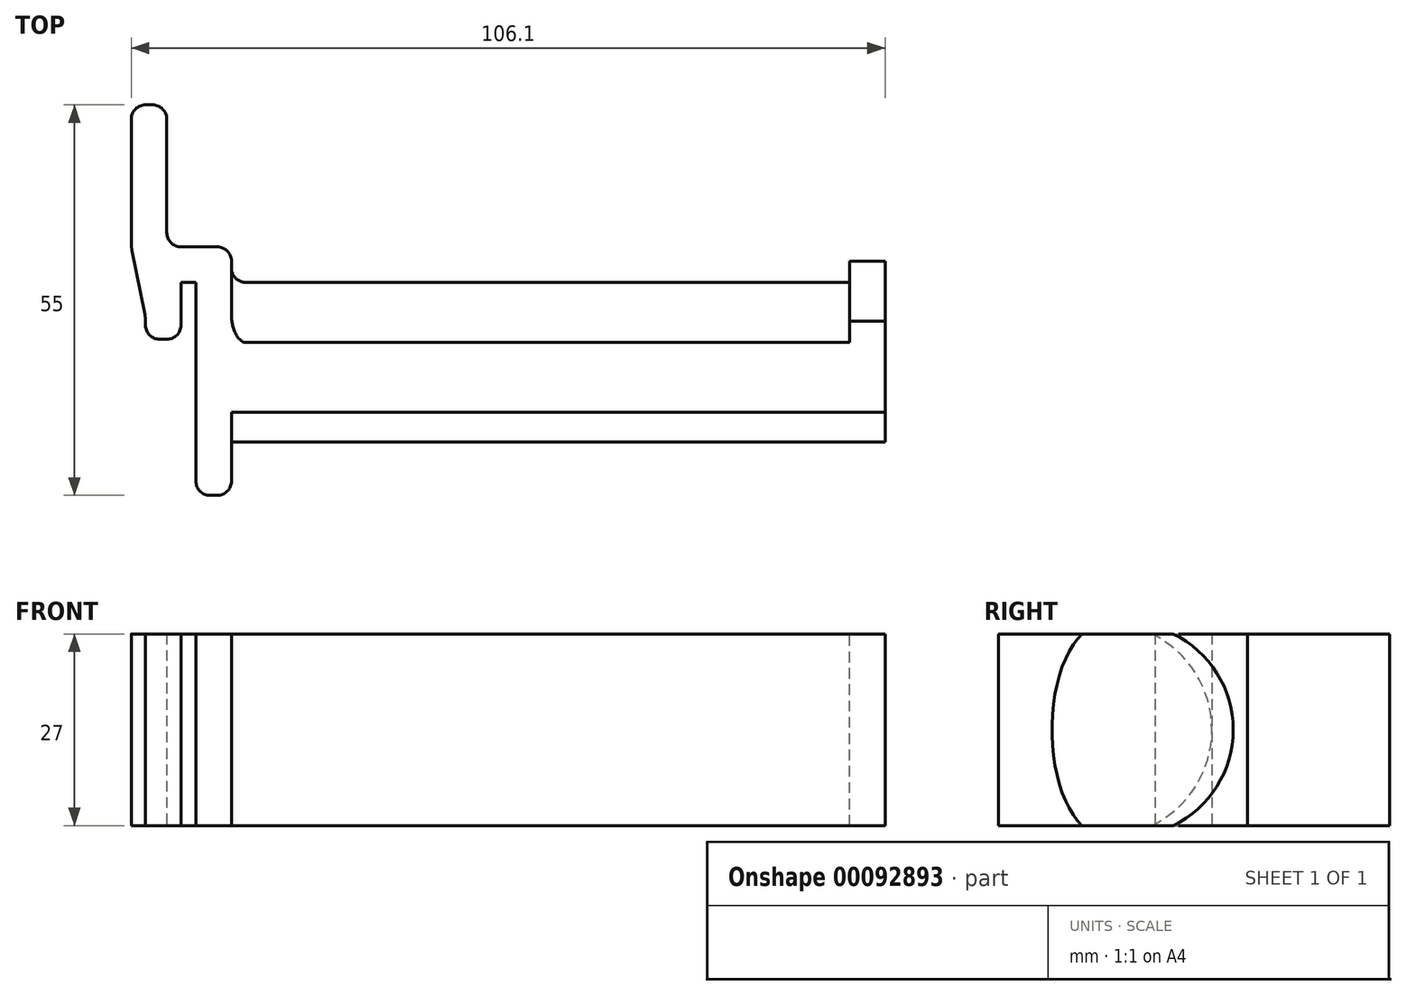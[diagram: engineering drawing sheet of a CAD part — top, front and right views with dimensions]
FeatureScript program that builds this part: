
annotation { "Feature Type Name" : "Feature", "Feature Type Description" : "" }
export const myFeature = defineFeature(function(context is Context, id is Id, definition is map)
    precondition{}
    {
        {
            assignVariable(context, id + "F0", {"name" : "Diameter", "anyValue" : 30});
        }
        {
            assignVariable(context, id + "F1", {"name" : "Width", "anyValue" : 85});
        }
        {
            var Q0;
            Q0=qCreatedBy(makeId("Top.planeOp"),FACE);
            var sketch = newSketch(context, id + "F2", { "sketchPlane" : qUnion([Q0])});
            skLineSegment(sketch, "E0", {"start": v(-10.1, -13) * mm, "end": v(-9.1, -13) * mm});
            skLineSegment(sketch, "E1", {"start": v(-7.1, -11) * mm, "end": v(-7.1, -5) * mm});
            skLineSegment(sketch, "E2", {"start": v(-7.1, -5) * mm, "end": v(-5, -5) * mm});
            skLineSegment(sketch, "E3", {"start": v(-5, -5) * mm, "end": v(-5, -33) * mm});
            skLineSegment(sketch, "E4", {"start": v(-3, -35) * mm, "end": v(-2, -35) * mm});
            skLineSegment(sketch, "E5", {"start": v(0, -33) * mm, "end": v(0, -2) * mm});
            skLineSegment(sketch, "E6", {"start": v(-2, 0) * mm, "end": v(-7.1, 0) * mm});
            skLineSegment(sketch, "E7", {"start": v(-9.1, 2) * mm, "end": v(-9.1, 18) * mm});
            skLineSegment(sketch, "E8", {"start": v(-11.1, 20) * mm, "end": v(-12.1, 20) * mm});
            skLineSegment(sketch, "E9", {"start": v(-14.1, 18) * mm, "end": v(-14.1, 0.5) * mm});
            skLineSegment(sketch, "E10", {"start": v(-12.1, -10.5) * mm, "end": v(-12.1, -11) * mm});
            skPoint(sketch, "E11.visualSharp", {"position": v(-9.1, 0) * mm});
            skArc(sketch, "E11.filletArc", {"start": v(-9.1, 2) * mm, "mid": v(-8.51, 0.59) * mm, "end": v(-7.1, 0) * mm});
            skPoint(sketch, "E12.visualSharp", {"position": v(0, 0) * mm});
            skArc(sketch, "E12.filletArc", {"start": v(0, -2) * mm, "mid": v(-0.59, -0.59) * mm, "end": v(-2, 0) * mm});
            skPoint(sketch, "E13.visualSharp", {"position": v(-9.1, 20) * mm});
            skArc(sketch, "E13.filletArc", {"start": v(-9.1, 18) * mm, "mid": v(-9.69, 19.41) * mm, "end": v(-11.1, 20) * mm});
            skPoint(sketch, "E14.visualSharp", {"position": v(-14.1, 20) * mm});
            skArc(sketch, "E14.filletArc", {"start": v(-12.1, 20) * mm, "mid": v(-13.51, 19.41) * mm, "end": v(-14.1, 18) * mm});
            skPoint(sketch, "E15.visualSharp", {"position": v(0, -35) * mm});
            skArc(sketch, "E15.filletArc", {"start": v(-2, -35) * mm, "mid": v(-0.59, -34.41) * mm, "end": v(0, -33) * mm});
            skPoint(sketch, "E16.visualSharp", {"position": v(-5, -35) * mm});
            skArc(sketch, "E16.filletArc", {"start": v(-5, -33) * mm, "mid": v(-4.41, -34.41) * mm, "end": v(-3, -35) * mm});
            skPoint(sketch, "E17.visualSharp", {"position": v(-7.1, -13) * mm});
            skArc(sketch, "E17.filletArc", {"start": v(-9.1, -13) * mm, "mid": v(-7.69, -12.41) * mm, "end": v(-7.1, -11) * mm});
            skPoint(sketch, "E18.visualSharp", {"position": v(-12.1, -13) * mm});
            skArc(sketch, "E18.filletArc", {"start": v(-12.1, -11) * mm, "mid": v(-11.51, -12.41) * mm, "end": v(-10.1, -13) * mm});
            skLineSegment(sketch, "E19", {"start": v(-14, -0.49) * mm, "end": v(-12.2, -9.51) * mm});
            skPoint(sketch, "E20", {"position": v(-13.1, -5) * mm});
            skPoint(sketch, "E21.visualSharp", {"position": v(-14.1, 0) * mm});
            skArc(sketch, "E21.filletArc", {"start": v(-14.1, 0.5) * mm, "mid": v(-14.08, 0) * mm, "end": v(-14, -0.49) * mm});
            skPoint(sketch, "E22.visualSharp", {"position": v(-12.1, -10) * mm});
            skArc(sketch, "E22.filletArc", {"start": v(-12.1, -10.5) * mm, "mid": v(-12.12, -10) * mm, "end": v(-12.2, -9.51) * mm});
            skSolve(sketch);
        }
        {
            var Q0;
            Q0 = qSketchRegion(id + "F2", true);
            extrude(context, id + "F3", {"entities" : qUnion([Q0]), "endBound" : BoundingType.SYMMETRIC, "depth" : (getVariable(context, 'Diameter') * 0.9) * mm});
        }
        {
            var Q0;
            Q0=makeQuery(id+"F3.opExtrude","SWEPT_FACE",FACE,{"disambiguationData":[OSD([sQuery(id+"F2.wireOp",EDGE,"E5")])]});
            var sketch = newSketch(context, id + "F4", { "sketchPlane" : qUnion([Q0])});
            skArc(sketch, "E23", {"start": v(-13.46, -13.5) * mm, "mid": v(-5, 0) * mm, "end": v(-13.46, 13.5) * mm});
            skEllipse(sketch, "E24", {"center": v(-20, 0) * mm, "majorRadius": 15 * mm, "minorRadius": 7.5 * mm, "majorAxis": v(0, -1)});
            skLineSegment(sketch, "E25", {"start": v(-13.46, 13.5) * mm, "end": v(-23.27, 13.5) * mm});
            skLineSegment(sketch, "E26", {"start": v(-13.46, -13.5) * mm, "end": v(-23.27, -13.5) * mm});
            skSolve(sketch);
        }
        {
            var Q0;
            {var subQ0=sQuery(id+"F4.wireOp",EDGE,"E25");var subQ1=sQuery(id+"F4.wireOp",EDGE,"E24");var subQ2=makeQuery(id+"F4.imprint","INTERSECT",VERTEX,{"derivedFrom":[subQ1,subQ0]});Q0=makeQuery(id+"F4.imprint","IMPRINT",FACE,{"disambiguationData":[TD([[makeQuery(id+"F4.imprint","IMPRINT",EDGE,{"disambiguationData":[TD([[subQ2,1.0]])],"derivedFrom":subQ1}),1.0]])]});}
            var Q1;
            {var subQ0=sQuery(id+"F4.wireOp",EDGE,"E23");Q1=makeQuery(id+"F4.imprint","IMPRINT",FACE,{"disambiguationData":[TD([[makeQuery(id+"F4.imprint","IMPRINT",EDGE,{"derivedFrom":subQ0}),1.0]])]});}
            extrude(context, id + "F5", {"entities" : qUnion([Q0, Q1]), "operationType" : NewBodyOperationType.ADD, "depth" : (getVariable(context, 'Width') + 7) * mm});
        }
        {
            var Q0;
            Q0=makeQuery(id+"F5.opExtrude","CAP_FACE",FACE,{"disambiguationData":[OSD([sQuery(id+"F4.wireOp",EDGE,"E23"),sQuery(id+"F4.wireOp",EDGE,"E24"),sQuery(id+"F4.wireOp",EDGE,"E25"),sQuery(id+"F4.wireOp",EDGE,"E26")])],"isStart":false});
            var sketch = newSketch(context, id + "F6", { "sketchPlane" : qUnion([Q0])});
            skLineSegment(sketch, "E27.0", {"start": v(-13.46, 13.5) * mm, "end": v(-2, 13.5) * mm});
            skLineSegment(sketch, "E28.0", {"start": v(-13.46, -13.5) * mm, "end": v(-2, -13.5) * mm});
            skArc(sketch, "E29", {"start": v(-10.46, -13.5) * mm, "mid": v(-2, 0) * mm, "end": v(-10.46, 13.5) * mm});
            skPoint(sketch, "E30", {"position": v(-20, 0) * mm});
            skSolve(sketch);
        }
        {
            var Q0;
            Q0 = qSketchRegion(id + "F6", true);
            var Q1;
            {var subQ2=sQuery(id+"F6.wireOp",EDGE,"E29");Q1=makeQuery(id+"F6.imprint","IMPRINT",FACE,{"disambiguationData":[TD([[makeQuery(id+"F6.imprint","IMPRINT",EDGE,{"derivedFrom":subQ2}),1.0]])]});}
            extrude(context, id + "F7", {"entities" : qUnion([Q0, Q1]), "operationType" : NewBodyOperationType.ADD, "oppositeDirection" : true, "depth" : 5 * mm});
        }
        {
            var Q0;
            Q0=makeQuery(id+"F5.opExtrude","CAP_EDGE",EDGE,{"disambiguationData":[OSD([sQuery(id+"F4.wireOp",EDGE,"E23")])],"isStart":true});
            var Q1;
            Q1=makeQuery(id+"F5.opExtrude","CAP_EDGE",EDGE,{"disambiguationData":[OSD([sQuery(id+"F4.wireOp",EDGE,"E24")])],"isStart":true});
            var Q2;
            Q2=makeQuery(id+"F7.opExtrude","CAP_EDGE",EDGE,{"disambiguationData":[OSD([sQuery(id+"F4.wireOp",EDGE,"E23")])],"isStart":false});
            fillet(context, id + "F8", {"entities" : qUnion([Q0, Q1, Q2]), "radius" : 2 * mm, "tangentPropagation" : true, "allowEdgeOverflow" : false});
        }
    });
